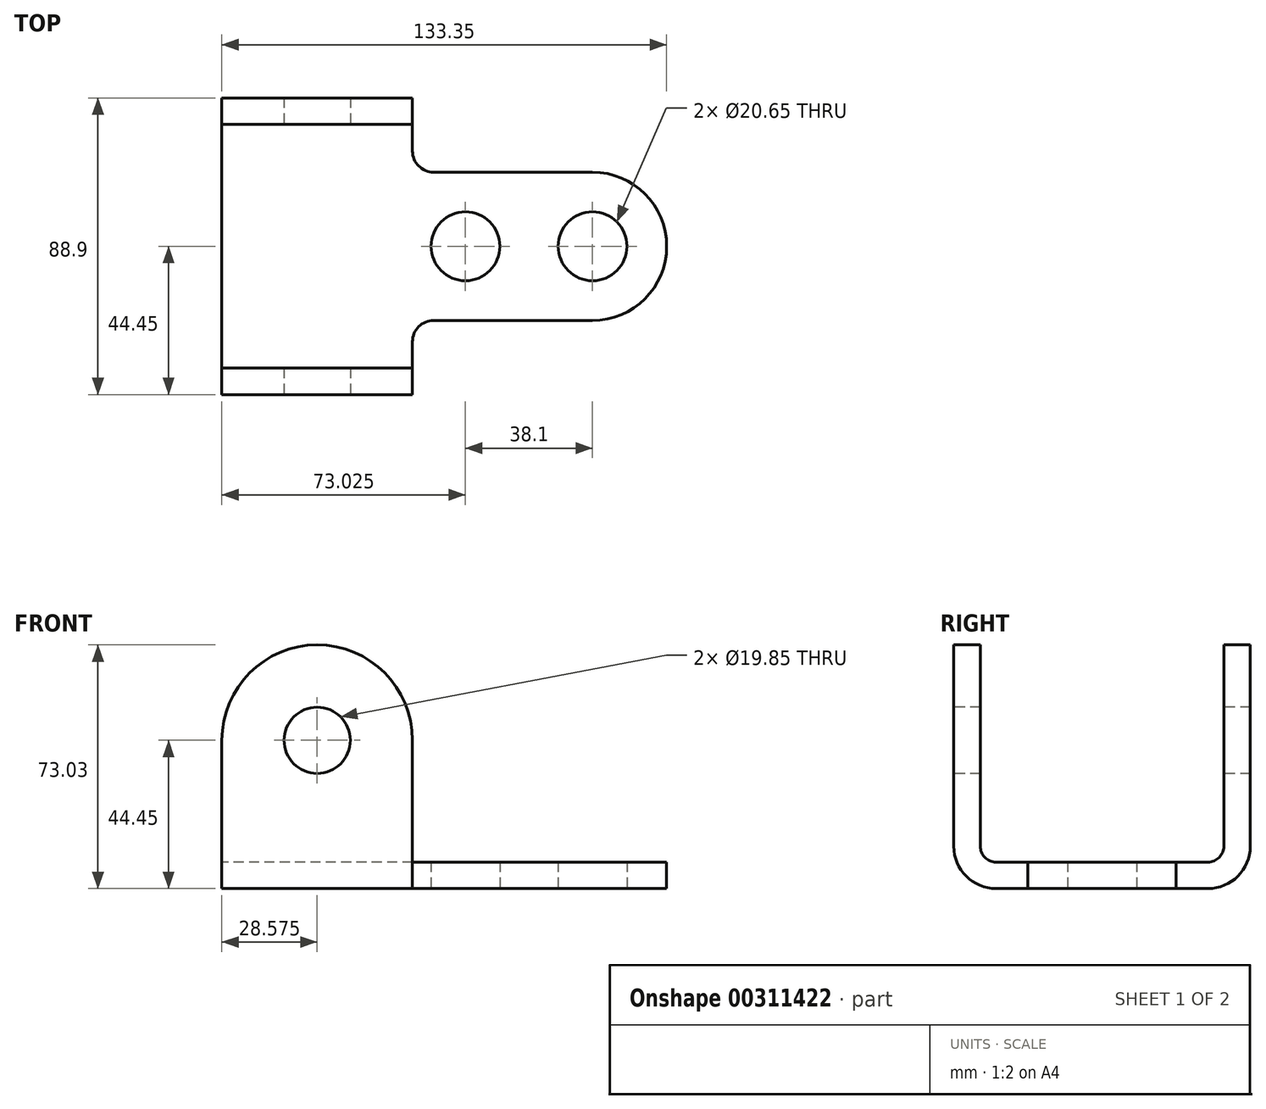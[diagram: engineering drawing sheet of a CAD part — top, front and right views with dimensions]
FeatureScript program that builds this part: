
annotation { "Feature Type Name" : "Feature", "Feature Type Description" : "" }
export const myFeature = defineFeature(function(context is Context, id is Id, definition is map)
    precondition{}
    {
        {
            var Q0;
            Q0=qCreatedBy(makeId("Right.planeOp"),FACE);
            var sketch = newSketch(context, id + "F0", { "sketchPlane" : qUnion([Q0])});
            skLineSegment(sketch, "E0", {"start": v(-44.45, 73.03) * mm, "end": v(-44.45, 12.7) * mm});
            skArc(sketch, "E1", {"start": v(-44.45, 12.7) * mm, "mid": v(-40.73, 3.72) * mm, "end": v(-31.75, 0) * mm});
            skLineSegment(sketch, "E2", {"start": v(-31.75, 0) * mm, "end": v(0, 0) * mm});
            skLineSegment(sketch, "E3", {"start": v(0, 0) * mm, "end": v(0, 7.94) * mm});
            skLineSegment(sketch, "E4", {"start": v(0, 7.94) * mm, "end": v(-31.75, 7.94) * mm});
            skArc(sketch, "E5", {"start": v(-36.51, 12.7) * mm, "mid": v(-35.12, 9.33) * mm, "end": v(-31.75, 7.94) * mm});
            skLineSegment(sketch, "E6", {"start": v(-36.51, 12.7) * mm, "end": v(-36.51, 73.03) * mm});
            skLineSegment(sketch, "E7", {"start": v(-36.51, 73.03) * mm, "end": v(-44.45, 73.03) * mm});
            skLineSegment(sketch, "E8.MirrorCS", {"start": v(0, 7.94) * mm, "end": v(31.75, 7.94) * mm});
            skArc(sketch, "E9.MirrorCS", {"start": v(36.51, 12.7) * mm, "mid": v(35.12, 9.33) * mm, "end": v(31.75, 7.94) * mm});
            skLineSegment(sketch, "E10.MirrorCS", {"start": v(36.51, 12.7) * mm, "end": v(36.51, 73.03) * mm});
            skLineSegment(sketch, "E11.MirrorCS", {"start": v(36.51, 73.03) * mm, "end": v(44.45, 73.03) * mm});
            skLineSegment(sketch, "E12.MirrorCS", {"start": v(44.45, 73.03) * mm, "end": v(44.45, 12.7) * mm});
            skArc(sketch, "E13.MirrorCS", {"start": v(44.45, 12.7) * mm, "mid": v(40.73, 3.72) * mm, "end": v(31.75, 0) * mm});
            skLineSegment(sketch, "E14.MirrorCS", {"start": v(31.75, 0) * mm, "end": v(0, 0) * mm});
            skSolve(sketch);
        }
        {
            var Q0;
            Q0 = qSketchRegion(id + "F0", true);
            extrude(context, id + "F1", {"entities" : qUnion([Q0]), "depth" : 57.15 * mm});
        }
        {
            var Q0;
            Q0=makeQuery(id+"F1.opExtrude","SWEPT_FACE",FACE,{"disambiguationData":[OSD([sQuery(id+"F0.wireOp",EDGE,"E0")])]});
            var sketch = newSketch(context, id + "F2", { "sketchPlane" : qUnion([Q0])});
            skCircle(sketch, "E15", {"center": v(28.58, 44.45) * mm, "radius": 9.92 * mm});
            skLineSegment(sketch, "E16", {"start": v(28.58, 73.03) * mm, "end": v(28.58, 0) * mm, "construction": true});
            skPoint(sketch, "E16.endSnap0", {"position": v(28.58, 12.7) * mm});
            skArc(sketch, "E17", {"start": v(57.15, 44.45) * mm, "mid": v(28.58, 73.03) * mm, "end": v(0, 44.45) * mm});
            skSolve(sketch);
        }
        {
            var Q0;
            Q0 = qSketchRegion(id + "F2", true);
            var Q1;
            {var subQ0=sQuery(id+"F2.wireOp",EDGE,"E17");var subQ1=sQuery(id+"F0.wireOp",EDGE,"E0");var subQ2=makeQuery(id+"F1.opExtrude","CAP_EDGE",EDGE,{"disambiguationData":[OSD([subQ1])],"isStart":false});var subQ3=makeQuery(id+"F2.imprint","INTERSECT",VERTEX,{"derivedFrom":[subQ2,subQ0]});Q1=makeQuery(id+"F2.imprint","IMPRINT",FACE,{"disambiguationData":[TD([[makeQuery(id+"F2.imprint","IMPRINT",EDGE,{"disambiguationData":[TD([[subQ3,-1.0]])],"derivedFrom":subQ0}),-1.0]])]});}
            var Q2;
            {var subQ0=sQuery(id+"F2.wireOp",EDGE,"E17");var subQ1=sQuery(id+"F0.wireOp",EDGE,"E0");var subQ2=makeQuery(id+"F1.opExtrude","CAP_EDGE",EDGE,{"disambiguationData":[OSD([subQ1])],"isStart":true});var subQ3=makeQuery(id+"F2.imprint","INTERSECT",VERTEX,{"derivedFrom":[subQ2,subQ0]});Q2=makeQuery(id+"F2.imprint","IMPRINT",FACE,{"disambiguationData":[TD([[makeQuery(id+"F2.imprint","IMPRINT",EDGE,{"disambiguationData":[TD([[subQ3,1.0]])],"derivedFrom":subQ0}),-1.0]])]});}
            extrude(context, id + "F3", {"entities" : qUnion([Q0, Q1, Q2]), "operationType" : NewBodyOperationType.REMOVE, "endBound" : BoundingType.THROUGH_ALL, "oppositeDirection" : true, "depth" : 25.4 * mm});
        }
        {
            var Q0;
            Q0=qCreatedBy(makeId("Top.planeOp"),FACE);
            var sketch = newSketch(context, id + "F4", { "sketchPlane" : qUnion([Q0])});
            skCircle(sketch, "E18", {"center": v(73.03, 0) * mm, "radius": 10.33 * mm});
            skCircle(sketch, "E19", {"center": v(111.12, 0) * mm, "radius": 10.33 * mm});
            skArc(sketch, "E20", {"start": v(57.15, 28.58) * mm, "mid": v(59, 24.08) * mm, "end": v(63.5, 22.23) * mm});
            skLineSegment(sketch, "E21", {"start": v(63.5, 22.23) * mm, "end": v(111.12, 22.23) * mm});
            skArc(sketch, "E22", {"start": v(111.12, -22.23) * mm, "mid": v(133.35, 0) * mm, "end": v(111.12, 22.23) * mm});
            skLineSegment(sketch, "E23", {"start": v(111.12, -22.22) * mm, "end": v(63.5, -22.23) * mm});
            skArc(sketch, "E24", {"start": v(63.5, -22.23) * mm, "mid": v(59, -24.08) * mm, "end": v(57.15, -28.58) * mm});
            skLineSegment(sketch, "E25", {"start": v(57.15, 28.58) * mm, "end": v(57.15, -28.58) * mm});
            skSolve(sketch);
        }
        {
            var Q0;
            Q0 = qSketchRegion(id + "F4", true);
            extrude(context, id + "F5", {"entities" : qUnion([Q0]), "operationType" : NewBodyOperationType.ADD, "depth" : 7.94 * mm});
        }
    });
